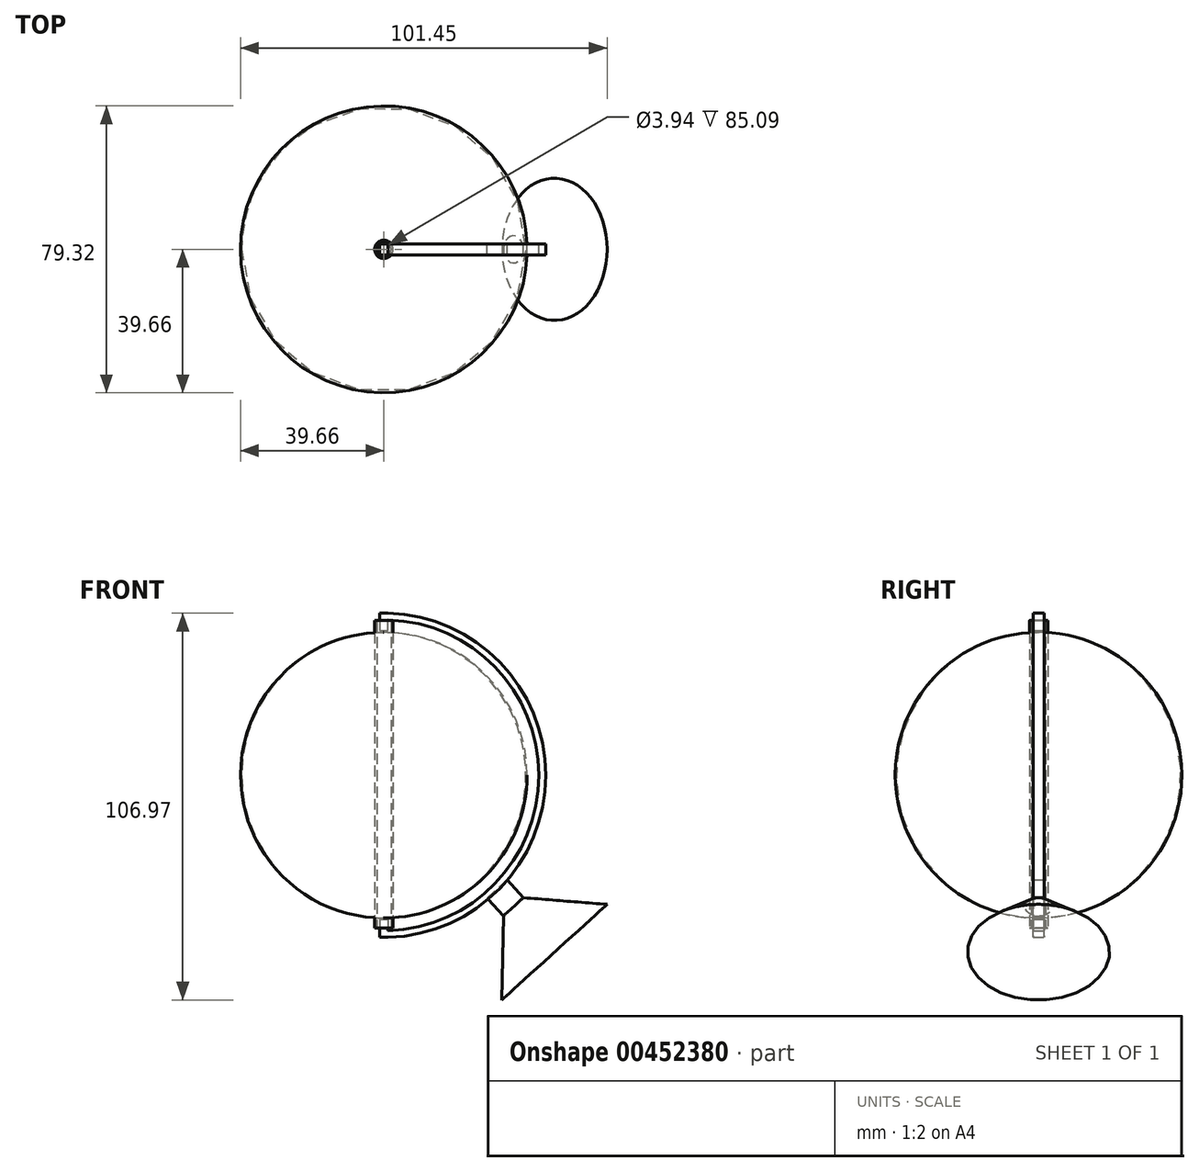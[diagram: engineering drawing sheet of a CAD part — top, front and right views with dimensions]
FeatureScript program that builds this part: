
annotation { "Feature Type Name" : "Feature", "Feature Type Description" : "" }
export const myFeature = defineFeature(function(context is Context, id is Id, definition is map)
    precondition{}
    {
        {
            var Q0;
            Q0=qCreatedBy(makeId("Front.planeOp"),FACE);
            var sketch = newSketch(context, id + "F0", { "sketchPlane" : qUnion([Q0])});
            skLineSegment(sketch, "E0", {"start": v(0, 34.54) * mm, "end": v(0, -44.45) * mm});
            skArc(sketch, "E1", {"start": v(0, -44.45) * mm, "mid": v(39.66, -4.96) * mm, "end": v(0, 34.54) * mm});
            skSolve(sketch);
        }
        {
            var Q0;
            Q0=makeQuery(id+"F0.imprint","IMPRINT",FACE,{"disambiguationData":[TD([[makeQuery(id+"F0.imprint","IMPRINT",EDGE,{"derivedFrom":sQuery(id+"F0.wireOp",EDGE,"E0")}),1.0]])]});
            var Q1;
            Q1=sQuery(id+"F0.wireOp",EDGE,"E0");
            revolve(context, id + "F1", {"entities" : qUnion([Q0]), "axis" : qUnion([Q1]), "revolveType" : RevolveType.FULL});
        }
        {
            var Q0;
            Q0=qCreatedBy(makeId("Top.planeOp"),FACE);
            var sketch = newSketch(context, id + "F2", { "sketchPlane" : qUnion([Q0])});
            skCircle(sketch, "E2", {"center": v(0, 0) * mm, "radius": 2.53 * mm});
            skCircle(sketch, "E3", {"center": v(0, 0) * mm, "radius": 1.97 * mm});
            skSolve(sketch);
        }
        {
            var Q0;
            Q0=makeQuery(id+"F2.imprint","IMPRINT",FACE,{"disambiguationData":[TD([[makeQuery(id+"F2.imprint","IMPRINT",EDGE,{"derivedFrom":sQuery(id+"F2.wireOp",EDGE,"E2")}),1.0]])]});
            extrude(context, id + "F3", {"entities" : qUnion([Q0]), "depth" : 37.85 * mm, "hasSecondDirection" : true, "secondDirectionOppositeDirection" : true, "secondDirectionDepth" : 47.24 * mm});
        }
        {
            var Q0;
            Q0=qCreatedBy(makeId("Front.planeOp"),FACE);
            var sketch = newSketch(context, id + "F4", { "sketchPlane" : qUnion([Q0])});
            skLineSegment(sketch, "E4", {"start": v(-1.18, 39.84) * mm, "end": v(-1.18, 35.02) * mm});
            skLineSegment(sketch, "E5", {"start": v(-1.18, 35.02) * mm, "end": v(1.15, 35.02) * mm});
            skLineSegment(sketch, "E6", {"start": v(1.15, 35.02) * mm, "end": v(1.15, 39.84) * mm});
            skLineSegment(sketch, "E7", {"start": v(1.15, 39.84) * mm, "end": v(-1.18, 39.84) * mm});
            skLineSegment(sketch, "E8", {"start": v(-1.18, -44.86) * mm, "end": v(-1.18, -49.8) * mm});
            skLineSegment(sketch, "E9", {"start": v(1.15, -44.86) * mm, "end": v(1.15, -49.8) * mm});
            skLineSegment(sketch, "E10", {"start": v(1.15, -49.8) * mm, "end": v(-1.18, -49.8) * mm});
            skLineSegment(sketch, "E11", {"start": v(-1.18, -44.86) * mm, "end": v(1.15, -44.86) * mm});
            skArc(sketch, "E12", {"start": v(1.15, -49.8) * mm, "mid": v(44.78, -4.98) * mm, "end": v(1.15, 39.84) * mm});
            skArc(sketch, "E13", {"start": v(1.15, -47.94) * mm, "mid": v(42.92, -4.98) * mm, "end": v(1.15, 37.98) * mm});
            skSolve(sketch);
        }
        {
            var Q0;
            Q0=makeQuery(id+"F4.imprint","IMPRINT",FACE,{"disambiguationData":[TD([[makeQuery(id+"F4.imprint","IMPRINT",EDGE,{"derivedFrom":sQuery(id+"F4.wireOp",EDGE,"E4")}),1.0]])]});
            var Q1;
            {var subQ0=sQuery(id+"F4.wireOp",EDGE,"E12");Q1=makeQuery(id+"F4.imprint","IMPRINT",FACE,{"disambiguationData":[TD([[makeQuery(id+"F4.imprint","IMPRINT",EDGE,{"derivedFrom":subQ0}),1.0]])]});}
            var Q2;
            Q2=makeQuery(id+"F4.imprint","IMPRINT",FACE,{"disambiguationData":[TD([[makeQuery(id+"F4.imprint","IMPRINT",EDGE,{"derivedFrom":sQuery(id+"F4.wireOp",EDGE,"E8")}),1.0]])]});
            extrude(context, id + "F5", {"entities" : qUnion([Q0, Q1, Q2]), "depth" : 1.52 * mm, "hasSecondDirection" : true, "secondDirectionOppositeDirection" : true, "secondDirectionDepth" : 1.55 * mm});
        }
        {
            var Q0;
            Q0=qCreatedBy(makeId("Front.planeOp"),FACE);
            var sketch = newSketch(context, id + "F6", { "sketchPlane" : qUnion([Q0])});
            skLineSegment(sketch, "E14", {"start": v(28.57, -38.96) * mm, "end": v(33.07, -43.91) * mm});
            skLineSegment(sketch, "E15", {"start": v(33.07, -43.91) * mm, "end": v(38.63, -38.86) * mm});
            skLineSegment(sketch, "E16", {"start": v(38.63, -38.86) * mm, "end": v(34.14, -33.9) * mm});
            skLineSegment(sketch, "E17", {"start": v(35.85, -41.39) * mm, "end": v(47.23, -53.91) * mm});
            skLineSegment(sketch, "E18", {"start": v(47.23, -53.91) * mm, "end": v(61.79, -40.69) * mm});
            skLineSegment(sketch, "E19", {"start": v(61.79, -40.69) * mm, "end": v(38.63, -38.86) * mm});
            skLineSegment(sketch, "E20", {"start": v(34.14, -33.9) * mm, "end": v(28.57, -38.96) * mm});
            skLineSegment(sketch, "E21", {"start": v(28.57, -38.96) * mm, "end": v(28.57, -38.96) * mm});
            skSolve(sketch);
        }
        {
            var Q0;
            {var subQ2=sQuery(id+"F6.wireOp",EDGE,"E17");Q0=makeQuery(id+"F6.imprint","IMPRINT",FACE,{"disambiguationData":[TD([[makeQuery(id+"F6.imprint","IMPRINT",EDGE,{"derivedFrom":subQ2}),1.0]])]});}
            var Q1;
            Q1=sQuery(id+"F6.wireOp",EDGE,"E17");
            revolve(context, id + "F7", {"entities" : qUnion([Q0]), "axis" : qUnion([Q1]), "revolveType" : RevolveType.FULL});
        }
        {
            var Q0;
            Q0=qCreatedBy(makeId("Front.planeOp"),FACE);
            var sketch = newSketch(context, id + "F8", { "sketchPlane" : qUnion([Q0])});
            skSolve(sketch);
        }
        {
            var Q0;
            {var subQ3=sQuery(id+"F6.wireOp",EDGE,"E14");Q0=makeQuery(id+"F6.imprint","IMPRINT",FACE,{"disambiguationData":[TD([[makeQuery(id+"F6.imprint","IMPRINT",EDGE,{"derivedFrom":subQ3}),1.0]])]});}
            var Q1;
            Q1 = qSketchRegion(id + "F8", true);
            extrude(context, id + "F9", {"entities" : qUnion([Q0, Q1]), "depth" : 1.47 * mm, "hasSecondDirection" : true, "secondDirectionOppositeDirection" : true, "secondDirectionDepth" : 1.55 * mm});
        }
    });
